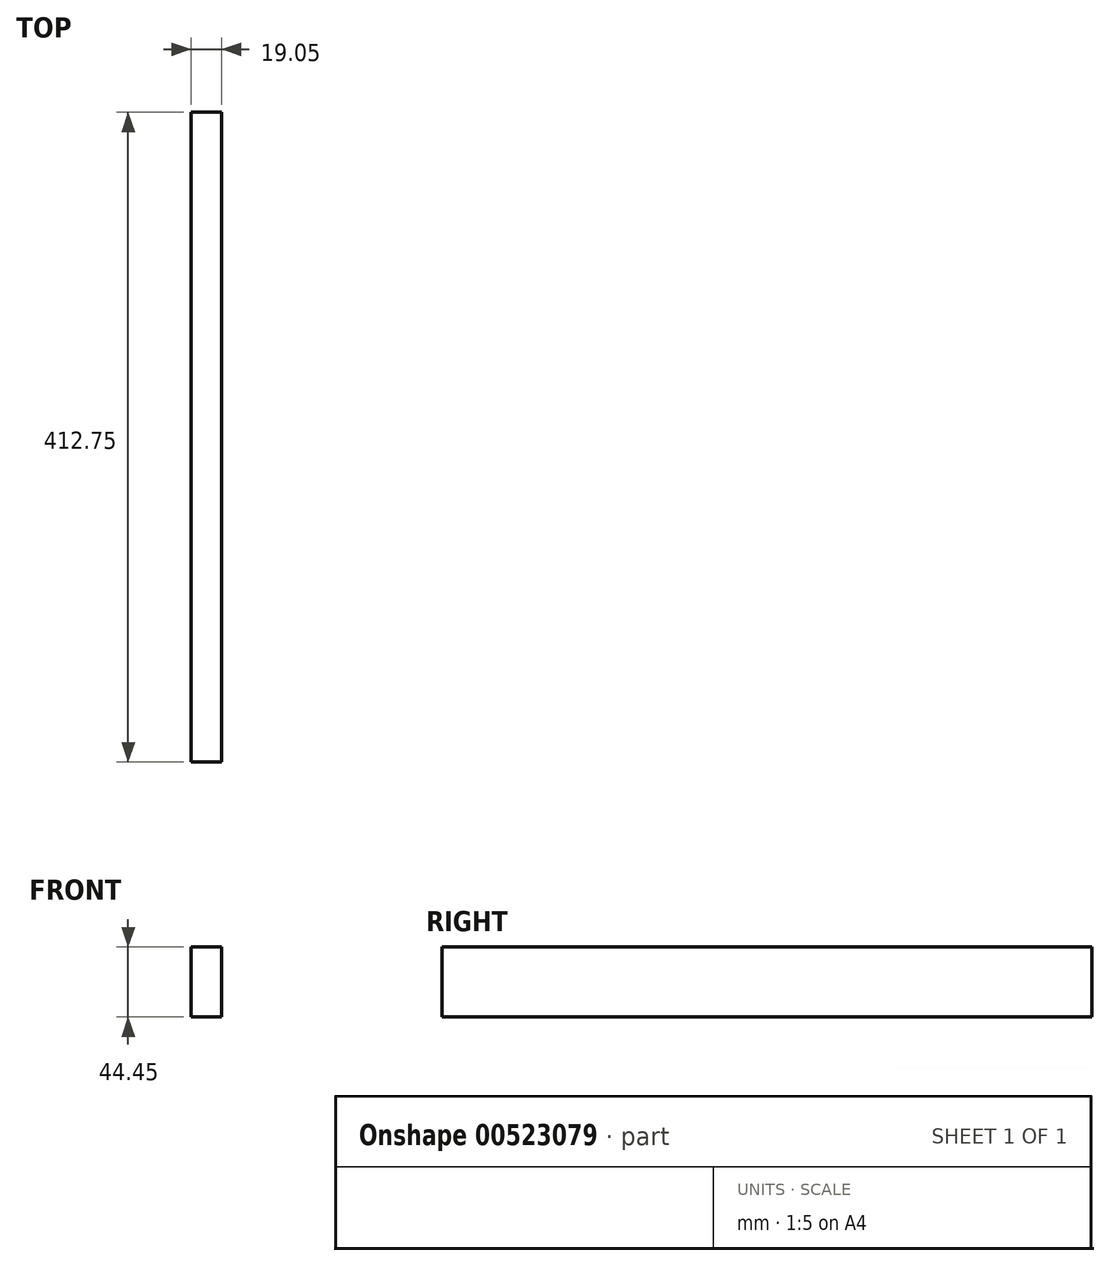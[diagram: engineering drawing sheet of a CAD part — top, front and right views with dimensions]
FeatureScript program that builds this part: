
annotation { "Feature Type Name" : "Feature", "Feature Type Description" : "" }
export const myFeature = defineFeature(function(context is Context, id is Id, definition is map)
    precondition{}
    {
        {
            var Q0;
            Q0=qCreatedBy(makeId("Front.planeOp"),FACE);
            var sketch = newSketch(context, id + "F0", { "sketchPlane" : qUnion([Q0])});
            skLineSegment(sketch, "E0.bottom", {"start": v(0, 0) * mm, "end": v(19.05, 0) * mm});
            skLineSegment(sketch, "E0.top", {"start": v(0, 44.45) * mm, "end": v(19.05, 44.45) * mm});
            skLineSegment(sketch, "E0.left", {"start": v(0, 0) * mm, "end": v(0, 44.45) * mm});
            skLineSegment(sketch, "E0.right", {"start": v(19.05, 0) * mm, "end": v(19.05, 44.45) * mm});
            skSolve(sketch);
        }
        {
            var Q0;
            Q0=qSketchRegion(id+"F0",true);
            extrude(context, id + "F1", {"entities" : qUnion([Q0]), "depth" : 412.75 * mm, "offsetDistance" : 25.4 * mm});
        }
    });
